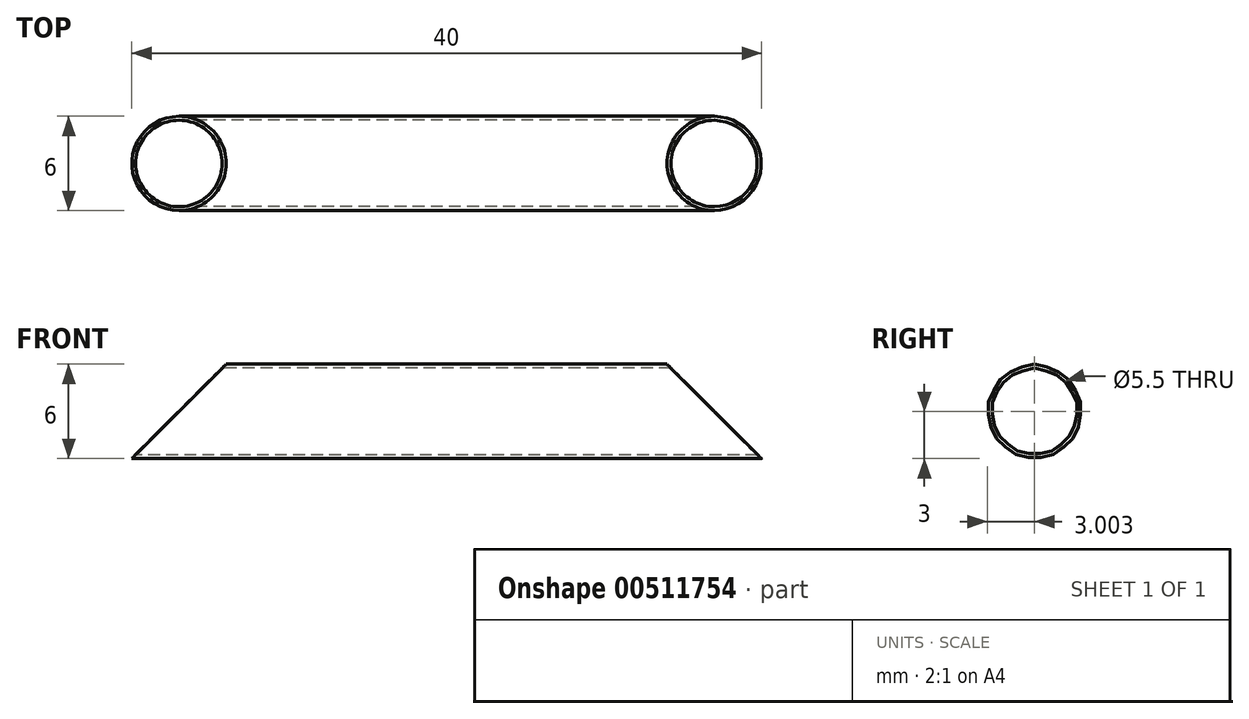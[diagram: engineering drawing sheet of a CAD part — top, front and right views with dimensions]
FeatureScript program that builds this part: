
annotation { "Feature Type Name" : "Feature", "Feature Type Description" : "" }
export const myFeature = defineFeature(function(context is Context, id is Id, definition is map)
    precondition{}
    {
        {
            var Q0;
            Q0=qCreatedBy(makeId("Top.planeOp"),FACE);
            var sketch = newSketch(context, id + "F0", { "sketchPlane" : qUnion([Q0])});
            skLineSegment(sketch, "E0.bottom", {"start": v(-38.84, -13.63) * mm, "end": v(1.16, -13.63) * mm});
            skLineSegment(sketch, "E0.top", {"start": v(-38.84, -19.63) * mm, "end": v(1.16, -19.63) * mm});
            skLineSegment(sketch, "E0.left", {"start": v(-38.84, -13.63) * mm, "end": v(-38.84, -19.63) * mm});
            skLineSegment(sketch, "E0.right", {"start": v(1.16, -13.63) * mm, "end": v(1.16, -19.63) * mm});
            skCircle(sketch, "E1", {"center": v(-8.52, -16.63) * mm, "radius": 3 * mm});
            skPoint(sketch, "E1.centerSnap0", {"position": v(1.16, -16.63) * mm});
            skSolve(sketch);
        }
        {
            var Q0;
            Q0=makeQuery(id+"F0.imprint","IMPRINT",FACE,{"disambiguationData":[TD([[makeQuery(id+"F0.imprint","IMPRINT",EDGE,{"derivedFrom":sQuery(id+"F0.wireOp",EDGE,"E0.bottom")}),-1.0]])]});
            var Q1;
            Q1=makeQuery(id+"F0.imprint","IMPRINT",FACE,{"disambiguationData":[TD([[makeQuery(id+"F0.imprint","IMPRINT",EDGE,{"derivedFrom":sQuery(id+"F0.wireOp",EDGE,"E1")}),1.0]])]});
            extrude(context, id + "F1", {"entities" : qUnion([Q0, Q1]), "depth" : 6 * mm, "offsetDistance" : 25 * mm});
        }
        {
            var Q0;
            Q0=makeQuery(id+"F1.opExtrude","SWEPT_FACE",FACE,{"disambiguationData":[OSD([sQuery(id+"F0.wireOp",EDGE,"E0.top")])]});
            var sketch = newSketch(context, id + "F2", { "sketchPlane" : qUnion([Q0])});
            skLineSegment(sketch, "E2", {"start": v(-4.84, 6) * mm, "end": v(1.16, 0) * mm});
            skLineSegment(sketch, "E3", {"start": v(-38.84, 0) * mm, "end": v(-32.84, 6) * mm});
            skSolve(sketch);
        }
        {
            var Q0;
            Q0 = qSketchRegion(id + "F2", true);
            var Q1;
            {var subQ0=sQuery(id+"F2.wireOp",EDGE,"E2");Q1=makeQuery(id+"F2.imprint","IMPRINT",FACE,{"disambiguationData":[TD([[makeQuery(id+"F2.imprint","IMPRINT",EDGE,{"derivedFrom":subQ0}),1.0]])]});}
            extrude(context, id + "F3", {"entities" : qUnion([Q0, Q1]), "operationType" : NewBodyOperationType.REMOVE, "endBound" : BoundingType.THROUGH_ALL, "oppositeDirection" : true, "depth" : 25 * mm, "offsetDistance" : 25 * mm});
        }
        {
            var Q0;
            Q0=makeQuery(id+"F1.opExtrude","SWEPT_FACE",FACE,{"disambiguationData":[OSD([sQuery(id+"F0.wireOp",EDGE,"E0.left")])]});
            var sketch = newSketch(context, id + "F4", { "sketchPlane" : qUnion([Q0])});
            skCircle(sketch, "E4", {"center": v(16.63, 3) * mm, "radius": 2.75 * mm});
            skPoint(sketch, "E4.centerSnap0", {"position": v(19.63, 3) * mm});
            skPoint(sketch, "E4.centerSnap1", {"position": v(16.63, 0) * mm});
            skSolve(sketch);
        }
        {
            var Q0;
            Q0=makeQuery(id+"F4.imprint","IMPRINT",FACE,{"disambiguationData":[TD([[makeQuery(id+"F4.imprint","IMPRINT",EDGE,{"derivedFrom":sQuery(id+"F4.wireOp",EDGE,"E4")}),1.0]])]});
            var Q1;
            Q1=sQuery(id+"F4.wireOp",EDGE,"E4");
            extrude(context, id + "F5", {"entities" : qUnion([Q0]), "operationType" : NewBodyOperationType.REMOVE, "surfaceEntities" : qUnion([Q1]), "endBound" : BoundingType.THROUGH_ALL, "oppositeDirection" : true, "depth" : 25 * mm, "offsetDistance" : 25 * mm});
        }
        {
            var Q0;
            Q0=makeQuery(id+"F1.opExtrude","CAP_EDGE",EDGE,{"disambiguationData":[OSD([sQuery(id+"F0.wireOp",EDGE,"E0.top")])],"isStart":false});
            var Q1;
            Q1=makeQuery(id+"F1.opExtrude","CAP_EDGE",EDGE,{"disambiguationData":[OSD([sQuery(id+"F0.wireOp",EDGE,"E0.bottom")])],"isStart":false});
            var Q2;
            Q2=makeQuery(id+"F1.opExtrude","CAP_EDGE",EDGE,{"disambiguationData":[OSD([sQuery(id+"F0.wireOp",EDGE,"E0.bottom")])],"isStart":true});
            var Q3;
            Q3=makeQuery(id+"F1.opExtrude","CAP_EDGE",EDGE,{"disambiguationData":[OSD([sQuery(id+"F0.wireOp",EDGE,"E0.top")])],"isStart":true});
            fillet(context, id + "F6", {"entities" : qUnion([Q0, Q1, Q2, Q3]), "radius" : 3 * mm, "tangentPropagation" : true, "allowEdgeOverflow" : false});
        }
        {
            var Q0;
            {var subQ0=sQuery(id+"F2.wireOp",EDGE,"E3");Q0=makeQuery(id+"F2.imprint","IMPRINT",FACE,{"disambiguationData":[TD([[makeQuery(id+"F2.imprint","IMPRINT",EDGE,{"derivedFrom":subQ0}),1.0]])]});}
            extrude(context, id + "F7", {"entities" : qUnion([Q0]), "operationType" : NewBodyOperationType.REMOVE, "endBound" : BoundingType.THROUGH_ALL, "oppositeDirection" : true, "depth" : 25 * mm, "offsetDistance" : 25 * mm});
        }
    });
